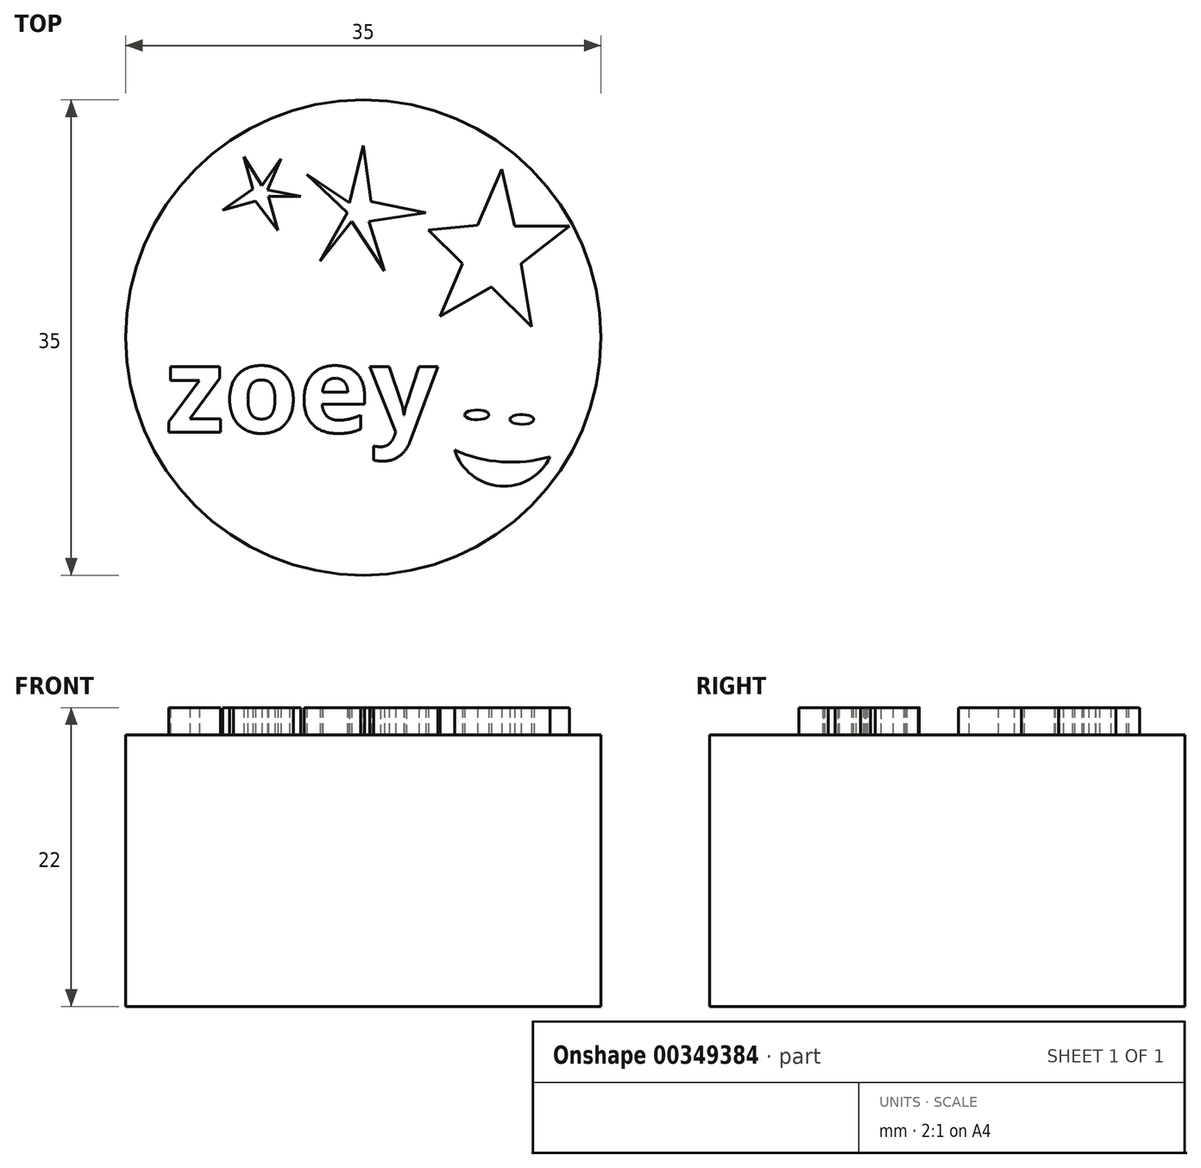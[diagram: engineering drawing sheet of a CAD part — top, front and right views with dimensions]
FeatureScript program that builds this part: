
annotation { "Feature Type Name" : "Feature", "Feature Type Description" : "" }
export const myFeature = defineFeature(function(context is Context, id is Id, definition is map)
    precondition{}
    {
        {
            var Q0;
            Q0=qCreatedBy(makeId("Top.planeOp"),FACE);
            var sketch = newSketch(context, id + "F0", { "sketchPlane" : qUnion([Q0])});
            skCircle(sketch, "E0", {"center": v(0, 0) * mm, "radius": 17.5 * mm});
            skSolve(sketch);
        }
        {
            var Q0;
            Q0=makeQuery(id+"F0.imprint","IMPRINT",FACE,{"disambiguationData":[TD([[makeQuery(id+"F0.imprint","IMPRINT",EDGE,{"derivedFrom":sQuery(id+"F0.wireOp",EDGE,"E0")}),1.0]])]});
            extrude(context, id + "F1", {"entities" : qUnion([Q0]), "depth" : 20 * mm});
        }
        {
            var Q0;
            Q0=makeQuery(id+"F1.opExtrude","CAP_FACE",FACE,{"disambiguationData":[OSD([sQuery(id+"F0.wireOp",EDGE,"E0")])],"isStart":false});
            var sketch = newSketch(context, id + "F2", { "sketchPlane" : qUnion([Q0])});
            skLineSegment(sketch, "E1", {"start": v(-8.12, 10.92) * mm, "end": v(-8.79, 13.32) * mm});
            skLineSegment(sketch, "E2", {"start": v(-8.79, 13.32) * mm, "end": v(-7.47, 11.2) * mm});
            skLineSegment(sketch, "E3", {"start": v(-7.47, 11.2) * mm, "end": v(-6.07, 13.16) * mm});
            skLineSegment(sketch, "E4", {"start": v(-6.07, 13.16) * mm, "end": v(-7.04, 10.88) * mm});
            skLineSegment(sketch, "E5", {"start": v(-7.04, 10.88) * mm, "end": v(-4.6, 10.4) * mm});
            skLineSegment(sketch, "E6", {"start": v(-4.6, 10.4) * mm, "end": v(-6.98, 10.4) * mm});
            skLineSegment(sketch, "E7", {"start": v(-6.98, 10.4) * mm, "end": v(-6.28, 7.87) * mm});
            skLineSegment(sketch, "E8", {"start": v(-6.28, 7.87) * mm, "end": v(-7.93, 10.04) * mm});
            skLineSegment(sketch, "E9", {"start": v(-7.93, 10.04) * mm, "end": v(-10.34, 9.37) * mm});
            skLineSegment(sketch, "E10", {"start": v(-10.34, 9.37) * mm, "end": v(-8.12, 10.92) * mm});
            skLineSegment(sketch, "E11", {"start": v(-1.02, 9.9) * mm, "end": v(-0.01, 14.14) * mm});
            skLineSegment(sketch, "E12", {"start": v(-0.01, 14.14) * mm, "end": v(0.57, 10.02) * mm});
            skLineSegment(sketch, "E13", {"start": v(0.57, 10.02) * mm, "end": v(4.6, 9.2) * mm});
            skLineSegment(sketch, "E14", {"start": v(4.6, 9.2) * mm, "end": v(0.4, 8.54) * mm});
            skLineSegment(sketch, "E15", {"start": v(0.4, 8.54) * mm, "end": v(1.57, 4.9) * mm});
            skLineSegment(sketch, "E16", {"start": v(1.57, 4.9) * mm, "end": v(-0.84, 8.54) * mm});
            skLineSegment(sketch, "E17", {"start": v(-0.84, 8.54) * mm, "end": v(-3.19, 5.63) * mm});
            skLineSegment(sketch, "E18", {"start": v(-3.19, 5.63) * mm, "end": v(-1.17, 9.2) * mm});
            skLineSegment(sketch, "E19", {"start": v(-1.17, 9.2) * mm, "end": v(-4.16, 12.03) * mm});
            skLineSegment(sketch, "E20", {"start": v(-4.16, 12.03) * mm, "end": v(-1.02, 9.9) * mm});
            skLineSegment(sketch, "E21", {"start": v(8.4, 8.25) * mm, "end": v(10.19, 12.4) * mm});
            skLineSegment(sketch, "E22", {"start": v(10.19, 12.4) * mm, "end": v(11.14, 8.2) * mm});
            skLineSegment(sketch, "E23", {"start": v(11.14, 8.2) * mm, "end": v(15.18, 8.2) * mm});
            skLineSegment(sketch, "E24", {"start": v(15.18, 8.2) * mm, "end": v(11.62, 5.46) * mm});
            skLineSegment(sketch, "E25", {"start": v(11.62, 5.46) * mm, "end": v(12.38, 0.8) * mm});
            skLineSegment(sketch, "E26", {"start": v(12.38, 0.8) * mm, "end": v(9.43, 3.74) * mm});
            skLineSegment(sketch, "E27", {"start": v(9.43, 3.74) * mm, "end": v(5.64, 1.57) * mm});
            skLineSegment(sketch, "E28", {"start": v(5.64, 1.57) * mm, "end": v(7.3, 5.44) * mm});
            skLineSegment(sketch, "E29", {"start": v(7.3, 5.44) * mm, "end": v(4.8, 7.93) * mm});
            skLineSegment(sketch, "E30", {"start": v(4.8, 7.93) * mm, "end": v(8.4, 8.25) * mm});
            skText(sketch, "E31", { "text": "zoey", "fontName": "OpenSans-Bold.ttf"});
            skArc(sketch, "E32", {"start": v(6.73, -8.28) * mm, "mid": v(10.07, -10.94) * mm, "end": v(13.76, -8.77) * mm});
            skArc(sketch, "E33", {"start": v(6.73, -8.28) * mm, "mid": v(10.2, -9.16) * mm, "end": v(13.76, -8.77) * mm});
            skEllipse(sketch, "E34", {"center": v(8.35, -5.69) * mm, "majorRadius": 0.9 * mm, "minorRadius": 0.36 * mm, "majorAxis": v(-1, 0)});
            skEllipse(sketch, "E35", {"center": v(11.67, -6.03) * mm, "majorRadius": 0.9 * mm, "minorRadius": 0.36 * mm, "majorAxis": v(-1, 0)});
            const initialGuessF2  = {"E31": [-0.01455, -0.00698, 1, 0, 0.00637]};
            skSetInitialGuess(sketch, initialGuessF2);
            skSolve(sketch);
        }
        {
            var Q0;
            Q0=makeQuery(id+"F2.imprint","IMPRINT",FACE,{"disambiguationData":[TD([[makeQuery(id+"F2.imprint","IMPRINT",EDGE,{"derivedFrom":sQuery(id+"F2.wireOp",EDGE,"E1")}),-1.0]])]});
            extrude(context, id + "F3", {"entities" : qUnion([Q0]), "operationType" : NewBodyOperationType.ADD, "depth" : 2 * mm});
        }
        {
            var Q0;
            Q0=makeQuery(id+"F2.imprint","IMPRINT",FACE,{"disambiguationData":[TD([[makeQuery(id+"F2.imprint","IMPRINT",EDGE,{"derivedFrom":sQuery(id+"F2.wireOp",EDGE,"E11")}),-1.0]])]});
            var Q1;
            Q1=makeQuery(id+"F2.imprint","IMPRINT",FACE,{"disambiguationData":[TD([[makeQuery(id+"F2.imprint","IMPRINT",EDGE,{"derivedFrom":sQuery(id+"F2.wireOp",EDGE,"E21")}),-1.0]])]});
            var Q2;
            Q2=makeQuery(id+"F2.imprint","IMPRINT",FACE,{"disambiguationData":[TD([[makeQuery(id+"F2.imprint","IMPRINT",EDGE,{"derivedFrom":sQuery(id+"F2.wireOp",EDGE,"E31.sketch_text.stroke-0")}),-1.0]])]});
            var Q3;
            Q3=makeQuery(id+"F2.imprint","IMPRINT",FACE,{"disambiguationData":[TD([[makeQuery(id+"F2.imprint","IMPRINT",EDGE,{"derivedFrom":sQuery(id+"F2.wireOp",EDGE,"E31.sketch_text.stroke-10")}),-1.0]])]});
            var Q4;
            Q4=makeQuery(id+"F2.imprint","IMPRINT",FACE,{"disambiguationData":[TD([[makeQuery(id+"F2.imprint","IMPRINT",EDGE,{"derivedFrom":sQuery(id+"F2.wireOp",EDGE,"E31.sketch_text.stroke-28")}),-1.0]])]});
            var Q5;
            Q5=makeQuery(id+"F2.imprint","IMPRINT",FACE,{"disambiguationData":[TD([[makeQuery(id+"F2.imprint","IMPRINT",EDGE,{"derivedFrom":sQuery(id+"F2.wireOp",EDGE,"E31.sketch_text.stroke-48")}),-1.0]])]});
            extrude(context, id + "F4", {"entities" : qUnion([Q0, Q1, Q2, Q3, Q4, Q5]), "operationType" : NewBodyOperationType.ADD, "depth" : 2 * mm});
        }
        {
            var Q0;
            Q0=makeQuery(id+"F2.imprint","IMPRINT",FACE,{"disambiguationData":[TD([[makeQuery(id+"F2.imprint","IMPRINT",EDGE,{"derivedFrom":sQuery(id+"F2.wireOp",EDGE,"E32")}),1.0]])]});
            var Q1;
            Q1=makeQuery(id+"F2.imprint","IMPRINT",FACE,{"disambiguationData":[TD([[makeQuery(id+"F2.imprint","IMPRINT",EDGE,{"derivedFrom":sQuery(id+"F2.wireOp",EDGE,"E34")}),1.0]])]});
            var Q2;
            Q2=makeQuery(id+"F2.imprint","IMPRINT",FACE,{"disambiguationData":[TD([[makeQuery(id+"F2.imprint","IMPRINT",EDGE,{"derivedFrom":sQuery(id+"F2.wireOp",EDGE,"E35")}),1.0]])]});
            extrude(context, id + "F5", {"entities" : qUnion([Q0, Q1, Q2]), "operationType" : NewBodyOperationType.ADD, "depth" : 2 * mm});
        }
    });
